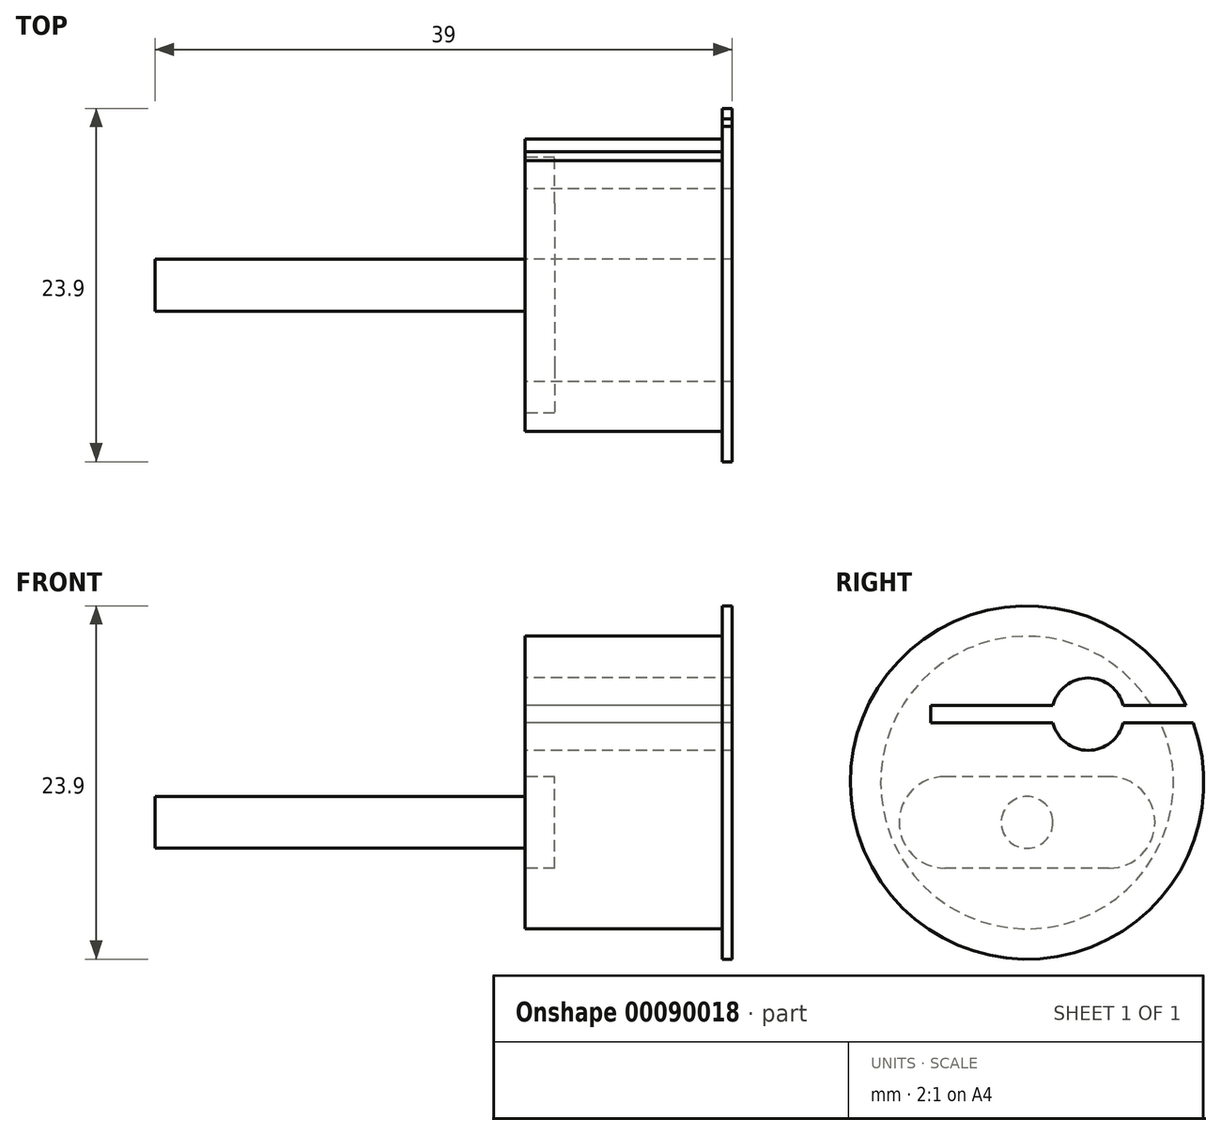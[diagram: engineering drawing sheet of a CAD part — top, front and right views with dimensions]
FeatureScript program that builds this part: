
annotation { "Feature Type Name" : "Feature", "Feature Type Description" : "" }
export const myFeature = defineFeature(function(context is Context, id is Id, definition is map)
    precondition{}
    {
        {
            var Q0;
            Q0=qCreatedBy(makeId("Front.planeOp"),FACE);
            var sketch = newSketch(context, id + "F0", { "sketchPlane" : qUnion([Q0])});
            skLineSegment(sketch, "E0", {"start": v(0, 0) * mm, "end": v(0, 11.95) * mm});
            skLineSegment(sketch, "E1", {"start": v(0, 11.95) * mm, "end": v(-0.65, 11.95) * mm});
            skLineSegment(sketch, "E2", {"start": v(-0.65, 11.95) * mm, "end": v(-0.65, 9.9) * mm});
            skLineSegment(sketch, "E3", {"start": v(-0.65, 9.9) * mm, "end": v(-14, 9.9) * mm});
            skLineSegment(sketch, "E4", {"start": v(-14, 9.9) * mm, "end": v(-14, 0) * mm});
            skLineSegment(sketch, "E5.MirrorCS", {"start": v(0, 0) * mm, "end": v(0, -11.95) * mm, "construction": true});
            skLineSegment(sketch, "E6.MirrorCS", {"start": v(-0.65, -11.95) * mm, "end": v(-0.65, -9.9) * mm, "construction": true});
            skLineSegment(sketch, "E7.MirrorCS", {"start": v(0, -11.95) * mm, "end": v(-0.65, -11.95) * mm, "construction": true});
            skLineSegment(sketch, "E8.MirrorCS", {"start": v(-14, -9.9) * mm, "end": v(-14, 0) * mm, "construction": true});
            skLineSegment(sketch, "E9.MirrorCS", {"start": v(-0.65, -9.9) * mm, "end": v(-14, -9.9) * mm, "construction": true});
            skLineSegment(sketch, "E10", {"start": v(-14, 0) * mm, "end": v(0, 0) * mm});
            skSolve(sketch);
        }
        {
            var Q0;
            Q0 = qSketchRegion(id + "F0", true);
            var Q1;
            Q1=sQuery(id+"F0.wireOp",EDGE,"E10");
            revolve(context, id + "F1", {"entities" : qUnion([Q0]), "axis" : qUnion([Q1]), "revolveType" : RevolveType.FULL});
        }
        {
            var Q0;
            Q0=makeQuery(id+"F1.opRevolve","SWEPT_FACE",FACE,{"disambiguationData":[OSD([sQuery(id+"F0.wireOp",EDGE,"E4")])]});
            var sketch = newSketch(context, id + "F2", { "sketchPlane" : qUnion([Q0])});
            skArc(sketch, "E11", {"start": v(-1.75, 5.2) * mm, "mid": v(-4.13, 7.08) * mm, "end": v(-6.51, 5.2) * mm});
            skLineSegment(sketch, "E12.bottom", {"start": v(6.52, 4.05) * mm, "end": v(-1.75, 4.05) * mm});
            skLineSegment(sketch, "E12.top", {"start": v(6.52, 5.2) * mm, "end": v(-1.75, 5.2) * mm});
            skLineSegment(sketch, "E12.left", {"start": v(6.52, 4.05) * mm, "end": v(6.52, 5.2) * mm});
            skLineSegment(sketch, "E12.right", {"start": v(-11.24, 4.05) * mm, "end": v(-11.24, 5.2) * mm});
            skPoint(sketch, "E12.middle", {"position": v(-2.36, 4.62) * mm});
            skLineSegment(sketch, "E13", {"start": v(6.52, 4.63) * mm, "end": v(11.02, 4.63) * mm, "construction": true});
            skLineSegment(sketch, "E14.trimOffspring", {"start": v(-6.51, 5.2) * mm, "end": v(-11.24, 5.2) * mm});
            skLineSegment(sketch, "E15.trimOffspring", {"start": v(-6.51, 4.05) * mm, "end": v(-11.24, 4.05) * mm});
            skArc(sketch, "E16.trimOffspring", {"start": v(-6.51, 4.05) * mm, "mid": v(-4.13, 2.17) * mm, "end": v(-1.75, 4.05) * mm});
            skLineSegment(sketch, "E17", {"start": v(-1.75, 5.2) * mm, "end": v(-1.75, 4.05) * mm, "construction": true});
            skSolve(sketch);
        }
        {
            var Q0;
            Q0 = qSketchRegion(id + "F2", true);
            extrude(context, id + "F3", {"entities" : qUnion([Q0]), "operationType" : NewBodyOperationType.REMOVE, "endBound" : BoundingType.THROUGH_ALL, "oppositeDirection" : true, "depth" : 25 * mm});
        }
        {
            var Q0;
            Q0 = qSketchRegion(id + "F2", true);
            extrude(context, id + "F4", {"entities" : qUnion([Q0]), "operationType" : NewBodyOperationType.REMOVE, "endBound" : BoundingType.THROUGH_ALL, "oppositeDirection" : true, "depth" : 25 * mm});
        }
        {
            var Q0;
            Q0=makeQuery(id+"F1.opRevolve","SWEPT_FACE",FACE,{"disambiguationData":[OSD([sQuery(id+"F0.wireOp",EDGE,"E4")])]});
            var sketch = newSketch(context, id + "F5", { "sketchPlane" : qUnion([Q0])});
            skLineSegment(sketch, "E18.bottom", {"start": v(5.55, 0.4) * mm, "end": v(-5.55, 0.4) * mm});
            skLineSegment(sketch, "E18.top", {"start": v(5.55, -5.8) * mm, "end": v(-5.55, -5.8) * mm});
            skLineSegment(sketch, "E18.left", {"start": v(5.55, 0.4) * mm, "end": v(5.55, -5.8) * mm, "construction": true});
            skLineSegment(sketch, "E18.right", {"start": v(-5.55, 0.4) * mm, "end": v(-5.55, -5.8) * mm, "construction": true});
            skPoint(sketch, "E18.middle", {"position": v(0, -2.7) * mm});
            skArc(sketch, "E19", {"start": v(-5.55, 0.4) * mm, "mid": v(-8.65, -2.7) * mm, "end": v(-5.55, -5.8) * mm});
            skArc(sketch, "E20", {"start": v(5.55, -5.8) * mm, "mid": v(8.65, -2.7) * mm, "end": v(5.55, 0.4) * mm});
            skSolve(sketch);
        }
        {
            var Q0;
            Q0 = qSketchRegion(id + "F5", true);
            extrude(context, id + "F6", {"entities" : qUnion([Q0]), "operationType" : NewBodyOperationType.REMOVE, "oppositeDirection" : true, "depth" : 2 * mm});
        }
        {
            var Q0;
            Q0 = qSketchRegion(id + "F5", true);
            var Q1;
            Q1=makeQuery(id+"F6.boolean.opBoolean","COPY",FACE,{"derivedFrom":makeQuery(id+"F6.opExtrude","CAP_FACE",FACE,{"disambiguationData":[OSD([sQuery(id+"F5.wireOp",EDGE,"E18.bottom"),sQuery(id+"F5.wireOp",EDGE,"E18.top"),sQuery(id+"F5.wireOp",EDGE,"E19"),sQuery(id+"F5.wireOp",EDGE,"E20")])],"isStart":false})});
            extrude(context, id + "F7", {"entities" : qUnion([Q0]), "endBound" : BoundingType.UP_TO_SURFACE, "oppositeDirection" : true, "endBoundEntityFace" : qUnion([Q1]), "depth" : 25 * mm});
        }
        {
            var Q0;
            Q0=makeQuery(id+"F7.opExtrude","CAP_FACE",FACE,{"disambiguationData":[OSD([sQuery(id+"F5.wireOp",EDGE,"E18.bottom"),sQuery(id+"F5.wireOp",EDGE,"E18.top"),sQuery(id+"F5.wireOp",EDGE,"E19"),sQuery(id+"F5.wireOp",EDGE,"E20")])],"isStart":true});
            var sketch = newSketch(context, id + "F8", { "sketchPlane" : qUnion([Q0])});
            skCircle(sketch, "E21", {"center": v(0, -2.7) * mm, "radius": 1.75 * mm});
            skSolve(sketch);
        }
        {
            var Q0;
            Q0 = qSketchRegion(id + "F8", true);
            extrude(context, id + "F9", {"entities" : qUnion([Q0]), "depth" : 25 * mm});
        }
    });
